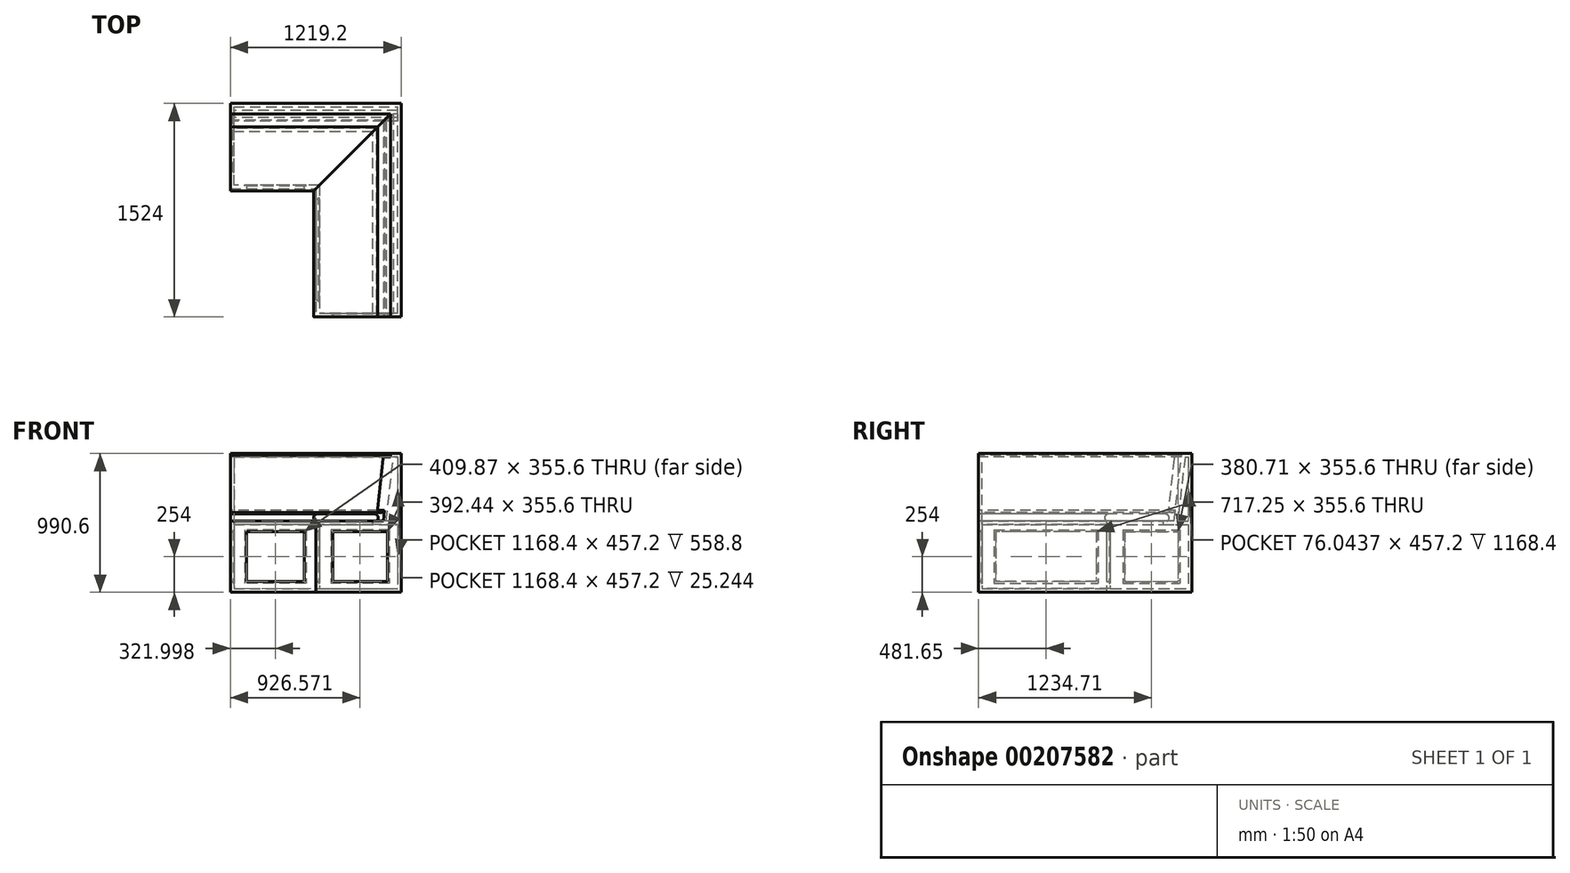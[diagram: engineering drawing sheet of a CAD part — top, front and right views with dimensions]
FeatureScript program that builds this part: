
annotation { "Feature Type Name" : "Feature", "Feature Type Description" : "" }
export const myFeature = defineFeature(function(context is Context, id is Id, definition is map)
    precondition{}
    {
        {
            var Q0;
            Q0=qCreatedBy(makeId("Top.planeOp"),FACE);
            var sketch = newSketch(context, id + "F0", { "sketchPlane" : qUnion([Q0])});
            skLineSegment(sketch, "E0", {"start": v(0, 0) * mm, "end": v(-1219.2, 0) * mm});
            skLineSegment(sketch, "E1", {"start": v(-1219.2, -609.6) * mm, "end": v(-609.6, -609.6) * mm});
            skLineSegment(sketch, "E2", {"start": v(-609.6, -609.6) * mm, "end": v(-609.6, -1524) * mm});
            skLineSegment(sketch, "E3", {"start": v(0, -1524) * mm, "end": v(0, 0) * mm});
            skLineSegment(sketch, "E4", {"start": v(-1219.2, -609.6) * mm, "end": v(-1219.2, -127) * mm});
            skLineSegment(sketch, "E5", {"start": v(-1219.2, -127) * mm, "end": v(-1219.2, 0) * mm});
            skLineSegment(sketch, "E6", {"start": v(-609.6, -1524) * mm, "end": v(-127, -1524) * mm});
            skLineSegment(sketch, "E7", {"start": v(-127, -1524) * mm, "end": v(0, -1524) * mm});
            skLineSegment(sketch, "E8", {"start": v(-1193.8, -584.2) * mm, "end": v(-584.2, -584.2) * mm});
            skLineSegment(sketch, "E9", {"start": v(-584.2, -584.2) * mm, "end": v(-584.2, -1498.6) * mm});
            skLineSegment(sketch, "E10", {"start": v(-584.2, -1498.6) * mm, "end": v(-25.4, -1498.6) * mm});
            skLineSegment(sketch, "E11", {"start": v(-25.4, -1498.6) * mm, "end": v(-25.4, -25.4) * mm});
            skLineSegment(sketch, "E12", {"start": v(-1193.8, -584.2) * mm, "end": v(-1193.8, -25.4) * mm});
            skLineSegment(sketch, "E13", {"start": v(-1193.8, -25.4) * mm, "end": v(-25.4, -25.4) * mm});
            skSolve(sketch);
        }
        {
            var Q0;
            Q0 = qSketchRegion(id + "F0", true);
            extrude(context, id + "F1", {"entities" : qUnion([Q0]), "depth" : 76.2 * mm});
        }
        {
            var Q0;
            Q0 = qSketchRegion(id + "F0", true);
            var Q1;
            Q1=makeQuery(id+"F0.imprint","IMPRINT",FACE,{"disambiguationData":[TD([[makeQuery(id+"F0.imprint","IMPRINT",EDGE,{"derivedFrom":sQuery(id+"F0.wireOp",EDGE,"E8")}),1.0]])]});
            extrude(context, id + "F2", {"entities" : qUnion([Q0, Q1]), "operationType" : NewBodyOperationType.ADD, "depth" : 25.4 * mm});
        }
        {
            var Q0;
            Q0=makeQuery(id+"F1.opExtrude","CAP_FACE",FACE,{"disambiguationData":[OSD([sQuery(id+"F0.wireOp",EDGE,"E0"),sQuery(id+"F0.wireOp",EDGE,"E1"),sQuery(id+"F0.wireOp",EDGE,"E2"),sQuery(id+"F0.wireOp",EDGE,"E3"),sQuery(id+"F0.wireOp",EDGE,"E4"),sQuery(id+"F0.wireOp",EDGE,"E5"),sQuery(id+"F0.wireOp",EDGE,"E6"),sQuery(id+"F0.wireOp",EDGE,"E7"),sQuery(id+"F0.wireOp",EDGE,"E8"),sQuery(id+"F0.wireOp",EDGE,"E9"),sQuery(id+"F0.wireOp",EDGE,"E10"),sQuery(id+"F0.wireOp",EDGE,"E11"),sQuery(id+"F0.wireOp",EDGE,"E12"),sQuery(id+"F0.wireOp",EDGE,"E13")])],"isStart":false});
            var sketch = newSketch(context, id + "F3", { "sketchPlane" : qUnion([Q0])});
            skLineSegment(sketch, "E14", {"start": v(-1219.2, -609.6) * mm, "end": v(-1219.2, -479.65) * mm});
            skLineSegment(sketch, "E15", {"start": v(-1219.2, -479.65) * mm, "end": v(-1193.8, -479.65) * mm});
            skLineSegment(sketch, "E16", {"start": v(-1193.8, -479.65) * mm, "end": v(-1193.8, -584.2) * mm});
            skLineSegment(sketch, "E17", {"start": v(-1193.8, -584.2) * mm, "end": v(-1102.14, -584.2) * mm});
            skLineSegment(sketch, "E18", {"start": v(-1102.14, -584.2) * mm, "end": v(-1102.14, -609.6) * mm});
            skLineSegment(sketch, "E19", {"start": v(-1102.14, -609.6) * mm, "end": v(-1219.2, -609.6) * mm});
            skLineSegment(sketch, "E20", {"start": v(-1219.2, 0) * mm, "end": v(-1219.2, -98.93) * mm});
            skLineSegment(sketch, "E21", {"start": v(-1219.2, -98.93) * mm, "end": v(-1193.8, -98.93) * mm});
            skLineSegment(sketch, "E22", {"start": v(-1193.8, -98.93) * mm, "end": v(-1193.8, -25.4) * mm});
            skLineSegment(sketch, "E23", {"start": v(-25.4, -25.4) * mm, "end": v(-1193.8, -25.4) * mm});
            skLineSegment(sketch, "E24", {"start": v(-609.6, -609.6) * mm, "end": v(-692.27, -609.6) * mm});
            skLineSegment(sketch, "E25", {"start": v(-692.27, -609.6) * mm, "end": v(-692.27, -584.2) * mm});
            skLineSegment(sketch, "E26", {"start": v(-692.27, -584.2) * mm, "end": v(-584.2, -584.2) * mm});
            skLineSegment(sketch, "E27", {"start": v(-584.2, -584.2) * mm, "end": v(-584.2, -683.73) * mm});
            skLineSegment(sketch, "E28", {"start": v(-584.2, -683.73) * mm, "end": v(-609.6, -683.73) * mm});
            skLineSegment(sketch, "E29", {"start": v(-609.6, -683.73) * mm, "end": v(-609.6, -609.6) * mm});
            skLineSegment(sketch, "E30", {"start": v(-609.6, -1524) * mm, "end": v(-609.6, -1400.97) * mm});
            skLineSegment(sketch, "E31", {"start": v(-609.6, -1400.97) * mm, "end": v(-584.2, -1400.97) * mm});
            skLineSegment(sketch, "E32", {"start": v(-584.2, -1400.97) * mm, "end": v(-584.2, -1498.6) * mm});
            skLineSegment(sketch, "E33", {"start": v(-584.2, -1498.6) * mm, "end": v(-488.85, -1498.6) * mm});
            skLineSegment(sketch, "E34", {"start": v(-488.85, -1498.6) * mm, "end": v(-488.85, -1524) * mm});
            skLineSegment(sketch, "E35", {"start": v(-488.85, -1524) * mm, "end": v(-609.6, -1524) * mm});
            skLineSegment(sketch, "E36", {"start": v(-25.4, -1498.6) * mm, "end": v(-96.4, -1498.6) * mm});
            skLineSegment(sketch, "E37", {"start": v(-96.4, -1498.6) * mm, "end": v(-96.4, -1524) * mm});
            skLineSegment(sketch, "E38", {"start": v(-96.4, -1524) * mm, "end": v(0, -1524) * mm});
            skLineSegment(sketch, "E39", {"start": v(-25.4, -25.4) * mm, "end": v(-25.4, -1498.6) * mm});
            skLineSegment(sketch, "E40", {"start": v(-1193.8, -25.4) * mm, "end": v(-1193.8, 0) * mm});
            skLineSegment(sketch, "E41", {"start": v(-1193.8, 0) * mm, "end": v(-1219.2, 0) * mm});
            skLineSegment(sketch, "E42", {"start": v(-25.4, -1498.6) * mm, "end": v(0, -1498.6) * mm});
            skLineSegment(sketch, "E43", {"start": v(0, -1498.6) * mm, "end": v(0, -1524) * mm});
            skLineSegment(sketch, "E44", {"start": v(0, -1498.6) * mm, "end": v(0, 0) * mm});
            skLineSegment(sketch, "E45", {"start": v(0, 0) * mm, "end": v(-25.4, 0) * mm});
            skLineSegment(sketch, "E46", {"start": v(-25.4, 0) * mm, "end": v(-25.4, -25.4) * mm});
            skLineSegment(sketch, "E47", {"start": v(-25.4, 0) * mm, "end": v(-1193.8, 0) * mm});
            skSolve(sketch);
        }
        {
            var Q0;
            Q0=makeQuery(id+"F3.imprint","IMPRINT",FACE,{"disambiguationData":[TD([[makeQuery(id+"F3.imprint","IMPRINT",EDGE,{"derivedFrom":sQuery(id+"F3.wireOp",EDGE,"E23")}),1.0]])]});
            var Q1;
            Q1=makeQuery(id+"F3.imprint","IMPRINT",FACE,{"disambiguationData":[TD([[makeQuery(id+"F3.imprint","IMPRINT",EDGE,{"derivedFrom":sQuery(id+"F3.wireOp",EDGE,"E39")}),-1.0]])]});
            extrude(context, id + "F4", {"entities" : qUnion([Q0, Q1]), "operationType" : NewBodyOperationType.ADD, "depth" : 889 * mm});
        }
        {
            var Q0;
            Q0=makeQuery(id+"F3.imprint","IMPRINT",FACE,{"disambiguationData":[TD([[makeQuery(id+"F3.imprint","IMPRINT",EDGE,{"derivedFrom":sQuery(id+"F3.wireOp",EDGE,"E14")}),-1.0]])]});
            var Q1;
            Q1=makeQuery(id+"F3.imprint","IMPRINT",FACE,{"disambiguationData":[TD([[makeQuery(id+"F3.imprint","IMPRINT",EDGE,{"derivedFrom":sQuery(id+"F3.wireOp",EDGE,"E20")}),-1.0]])]});
            var Q2;
            Q2=makeQuery(id+"F3.imprint","IMPRINT",FACE,{"disambiguationData":[TD([[makeQuery(id+"F3.imprint","IMPRINT",EDGE,{"derivedFrom":sQuery(id+"F3.wireOp",EDGE,"E24")}),1.0]])]});
            var Q3;
            Q3=makeQuery(id+"F3.imprint","IMPRINT",FACE,{"disambiguationData":[TD([[makeQuery(id+"F3.imprint","IMPRINT",EDGE,{"derivedFrom":sQuery(id+"F3.wireOp",EDGE,"E30")}),1.0]])]});
            var Q4;
            Q4=makeQuery(id+"F3.imprint","IMPRINT",FACE,{"disambiguationData":[TD([[makeQuery(id+"F3.imprint","IMPRINT",EDGE,{"derivedFrom":sQuery(id+"F3.wireOp",EDGE,"E36")}),-1.0]])]});
            extrude(context, id + "F5", {"entities" : qUnion([Q0, Q1, Q2, Q3, Q4]), "operationType" : NewBodyOperationType.ADD, "depth" : 355.6 * mm});
        }
        {
            var Q0;
            Q0=makeQuery(id+"F5.opExtrude","CAP_FACE",FACE,{"disambiguationData":[OSD([sQuery(id+"F3.wireOp",EDGE,"E24"),sQuery(id+"F3.wireOp",EDGE,"E25"),sQuery(id+"F3.wireOp",EDGE,"E26"),sQuery(id+"F3.wireOp",EDGE,"E27"),sQuery(id+"F3.wireOp",EDGE,"E28"),sQuery(id+"F3.wireOp",EDGE,"E29")])],"isStart":false});
            var sketch = newSketch(context, id + "F6", { "sketchPlane" : qUnion([Q0])});
            skLineSegment(sketch, "E48", {"start": v(-584.2, -584.2) * mm, "end": v(-1193.8, -584.2) * mm});
            skLineSegment(sketch, "E49", {"start": v(-1193.8, -584.2) * mm, "end": v(-1193.8, 0) * mm});
            skLineSegment(sketch, "E50", {"start": v(-1193.8, 0) * mm, "end": v(-1219.2, 0) * mm});
            skLineSegment(sketch, "E51", {"start": v(-1219.2, 0) * mm, "end": v(-1219.2, -609.6) * mm});
            skLineSegment(sketch, "E52", {"start": v(-1219.2, -609.6) * mm, "end": v(-609.6, -609.6) * mm});
            skLineSegment(sketch, "E53", {"start": v(-609.6, -609.6) * mm, "end": v(-609.6, -1524) * mm});
            skLineSegment(sketch, "E54", {"start": v(-609.6, -1524) * mm, "end": v(0, -1524) * mm});
            skLineSegment(sketch, "E55", {"start": v(0, -1524) * mm, "end": v(0, -1498.6) * mm});
            skLineSegment(sketch, "E56", {"start": v(0, -1498.6) * mm, "end": v(-584.2, -1498.6) * mm});
            skLineSegment(sketch, "E57", {"start": v(-584.2, -1498.6) * mm, "end": v(-584.2, -584.2) * mm});
            skSolve(sketch);
        }
        {
            var Q0;
            {var subQ1=sQuery(id+"F6.wireOp",EDGE,"E49");Q0=makeQuery(id+"F6.imprint","IMPRINT",FACE,{"disambiguationData":[TD([[makeQuery(id+"F6.imprint","IMPRINT",EDGE,{"derivedFrom":subQ1}),1.0]])]});}
            var Q1;
            {var subQ7=makeQuery(id+"F5.opExtrude","CAP_EDGE",EDGE,{"disambiguationData":[OSD([sQuery(id+"F3.wireOp",EDGE,"E25")])],"isStart":false});Q1=makeQuery(id+"F6.imprint","IMPRINT",FACE,{"disambiguationData":[TD([[makeQuery(id+"F6.imprint","IMPRINT",EDGE,{"derivedFrom":subQ7}),-1.0]])]});}
            var Q2;
            {var subQ2=sQuery(id+"F6.wireOp",EDGE,"E54");Q2=makeQuery(id+"F6.imprint","IMPRINT",FACE,{"disambiguationData":[TD([[makeQuery(id+"F6.imprint","IMPRINT",EDGE,{"derivedFrom":subQ2}),1.0]])]});}
            extrude(context, id + "F7", {"entities" : qUnion([Q0, Q1, Q2]), "operationType" : NewBodyOperationType.ADD, "depth" : 76.2 * mm});
        }
        {
            var Q0;
            Q0=makeQuery(id+"F7.boolean.opBoolean","MERGE",FACE,{"derivedFrom":[makeQuery(id+"F5.boolean.opBoolean","MERGE",FACE,{"derivedFrom":[makeQuery(id+"F1.opExtrude","SWEPT_FACE",FACE,{"disambiguationData":[OSD([sQuery(id+"F0.wireOp",EDGE,"E6"),sQuery(id+"F0.wireOp",EDGE,"E7")])]}),makeQuery(id+"F5.opExtrude","SWEPT_FACE",FACE,{"disambiguationData":[OSD([sQuery(id+"F3.wireOp",EDGE,"E35")])]}),makeQuery(id+"F5.opExtrude","SWEPT_FACE",FACE,{"disambiguationData":[OSD([sQuery(id+"F3.wireOp",EDGE,"E38")])]})]}),makeQuery(id+"F7.opExtrude","SWEPT_FACE",FACE,{"disambiguationData":[OSD([sQuery(id+"F6.wireOp",EDGE,"E54")])]})]});
            var sketch = newSketch(context, id + "F8", { "sketchPlane" : qUnion([Q0])});
            skLineSegment(sketch, "E58", {"start": v(0, 965.2) * mm, "end": v(-76.2, 965.2) * mm});
            skLineSegment(sketch, "E59", {"start": v(-76.2, 965.2) * mm, "end": v(-127, 508) * mm});
            skLineSegment(sketch, "E60", {"start": v(-127, 508) * mm, "end": v(0, 508) * mm});
            skLineSegment(sketch, "E61", {"start": v(0, 508) * mm, "end": v(0, 965.2) * mm});
            skLineSegment(sketch, "E62", {"start": v(-76.2, 965.2) * mm, "end": v(-54.4, 965.2) * mm});
            skLineSegment(sketch, "E63", {"start": v(-54.4, 965.2) * mm, "end": v(-105.2, 508) * mm});
            skLineSegment(sketch, "E64", {"start": v(-105.2, 508) * mm, "end": v(-127, 508) * mm});
            skSolve(sketch);
        }
        {
            var Q0;
            Q0 = qSketchRegion(id + "F8", true);
            extrude(context, id + "F9", {"entities" : qUnion([Q0]), "operationType" : NewBodyOperationType.ADD, "oppositeDirection" : true, "depth" : 25.4 * mm});
        }
        {
            var Q0;
            Q0=makeQuery(id+"F7.boolean.opBoolean","MERGE",FACE,{"derivedFrom":[makeQuery(id+"F5.boolean.opBoolean","MERGE",FACE,{"derivedFrom":[makeQuery(id+"F1.opExtrude","SWEPT_FACE",FACE,{"disambiguationData":[OSD([sQuery(id+"F0.wireOp",EDGE,"E4"),sQuery(id+"F0.wireOp",EDGE,"E5")])]}),makeQuery(id+"F5.opExtrude","SWEPT_FACE",FACE,{"disambiguationData":[OSD([sQuery(id+"F3.wireOp",EDGE,"E14")])]}),makeQuery(id+"F5.opExtrude","SWEPT_FACE",FACE,{"disambiguationData":[OSD([sQuery(id+"F3.wireOp",EDGE,"E20")])]})]}),makeQuery(id+"F7.opExtrude","SWEPT_FACE",FACE,{"disambiguationData":[OSD([sQuery(id+"F6.wireOp",EDGE,"E51")])]})]});
            var sketch = newSketch(context, id + "F10", { "sketchPlane" : qUnion([Q0])});
            skLineSegment(sketch, "E65", {"start": v(0, 965.2) * mm, "end": v(0, 508) * mm});
            skLineSegment(sketch, "E66", {"start": v(0, 508) * mm, "end": v(127, 508) * mm});
            skLineSegment(sketch, "E67", {"start": v(127, 508) * mm, "end": v(76.2, 965.2) * mm});
            skLineSegment(sketch, "E68", {"start": v(76.2, 965.2) * mm, "end": v(0, 965.2) * mm});
            skLineSegment(sketch, "E69", {"start": v(76.2, 965.2) * mm, "end": v(50.64, 965.2) * mm});
            skLineSegment(sketch, "E70", {"start": v(50.64, 965.2) * mm, "end": v(101.44, 508) * mm});
            skLineSegment(sketch, "E71", {"start": v(101.44, 508) * mm, "end": v(127, 508) * mm});
            skSolve(sketch);
        }
        {
            var Q0;
            Q0 = qSketchRegion(id + "F10", true);
            extrude(context, id + "F11", {"entities" : qUnion([Q0]), "operationType" : NewBodyOperationType.ADD, "oppositeDirection" : true, "depth" : 25.4 * mm});
        }
        {
            var Q0;
            Q0=makeQuery(id+"F7.opExtrude","CAP_FACE",FACE,{"disambiguationData":[OSD([sQuery(id+"F6.wireOp",EDGE,"E48"),sQuery(id+"F6.wireOp",EDGE,"E49"),sQuery(id+"F6.wireOp",EDGE,"E50"),sQuery(id+"F6.wireOp",EDGE,"E51"),sQuery(id+"F6.wireOp",EDGE,"E52"),sQuery(id+"F6.wireOp",EDGE,"E53"),sQuery(id+"F6.wireOp",EDGE,"E54"),sQuery(id+"F6.wireOp",EDGE,"E55"),sQuery(id+"F6.wireOp",EDGE,"E56"),sQuery(id+"F6.wireOp",EDGE,"E57")])],"isStart":false});
            var sketch = newSketch(context, id + "F12", { "sketchPlane" : qUnion([Q0])});
            skLineSegment(sketch, "E72", {"start": v(-1193.8, -203.2) * mm, "end": v(-1193.8, 0) * mm});
            skLineSegment(sketch, "E73", {"start": v(-1193.8, 0) * mm, "end": v(0, 0) * mm});
            skLineSegment(sketch, "E74", {"start": v(0, 0) * mm, "end": v(0, -1498.6) * mm});
            skLineSegment(sketch, "E75", {"start": v(0, -1498.6) * mm, "end": v(-203.2, -1498.6) * mm});
            skLineSegment(sketch, "E76", {"start": v(-203.2, -1498.6) * mm, "end": v(-203.2, -203.2) * mm});
            skLineSegment(sketch, "E77", {"start": v(-203.2, -203.2) * mm, "end": v(-1193.8, -203.2) * mm});
            skSolve(sketch);
        }
        {
            var Q0;
            Q0 = qSketchRegion(id + "F12", true);
            extrude(context, id + "F13", {"entities" : qUnion([Q0]), "operationType" : NewBodyOperationType.ADD, "oppositeDirection" : true, "depth" : 25.4 * mm});
        }
        {
            var Q0;
            Q0=makeQuery(id+"F10.imprint","IMPRINT",FACE,{"disambiguationData":[TD([[makeQuery(id+"F10.imprint","IMPRINT",EDGE,{"derivedFrom":sQuery(id+"F10.wireOp",EDGE,"E67")}),1.0]])]});
            var Q1;
            {var subQ0=sQuery(id+"F8.wireOp",EDGE,"E58");var subQ4=sQuery(id+"F3.wireOp",EDGE,"E39");Q1=makeQuery(id+"F13.boolean.opBoolean","SPLIT",FACE,{"disambiguationData":[TD([makeQuery(id+"F9.opExtrude","SWEPT_FACE",FACE,{"disambiguationData":[OSD([subQ0])]})])],"derivedFrom":makeQuery(id+"F4.boolean.opBoolean","MERGE",FACE,{"derivedFrom":[makeQuery(id+"F1.opExtrude","SWEPT_FACE",FACE,{"disambiguationData":[OSD([sQuery(id+"F0.wireOp",EDGE,"E11")])]}),makeQuery(id+"F4.opExtrude","SWEPT_FACE",FACE,{"disambiguationData":[OSD([subQ4])]})]})});}
            extrude(context, id + "F14", {"entities" : qUnion([Q0]), "operationType" : NewBodyOperationType.ADD, "endBound" : BoundingType.UP_TO_SURFACE, "oppositeDirection" : true, "endBoundEntityFace" : qUnion([Q1]), "depth" : 25.4 * mm});
        }
        {
            var Q0;
            Q0=makeQuery(id+"F8.imprint","IMPRINT",FACE,{"disambiguationData":[TD([[makeQuery(id+"F8.imprint","IMPRINT",EDGE,{"derivedFrom":sQuery(id+"F8.wireOp",EDGE,"E59")}),1.0]])]});
            var Q1;
            {var subQ0=sQuery(id+"F10.wireOp",EDGE,"E67");Q1=makeQuery(id+"F14.boolean.opBoolean","MERGE",FACE,{"derivedFrom":[makeQuery(id+"F11.opExtrude","SWEPT_FACE",FACE,{"disambiguationData":[OSD([subQ0])]}),makeQuery(id+"F14.opExtrude","SWEPT_FACE",FACE,{"disambiguationData":[OSD([subQ0])]})]});}
            extrude(context, id + "F15", {"entities" : qUnion([Q0]), "operationType" : NewBodyOperationType.ADD, "endBound" : BoundingType.UP_TO_SURFACE, "oppositeDirection" : true, "endBoundEntityFace" : qUnion([Q1]), "depth" : 25.4 * mm});
        }
        {
            var Q0;
            {var subQ9=sQuery(id+"F6.wireOp",EDGE,"E49");var subQ19=sQuery(id+"F0.wireOp",EDGE,"E8");var subQ21=sQuery(id+"F0.wireOp",EDGE,"E12");var subQ27=sQuery(id+"F10.wireOp",EDGE,"E65");Q0=makeQuery(id+"F13.boolean.opBoolean","SPLIT",FACE,{"disambiguationData":[TD([makeQuery(id+"F1.opExtrude","SWEPT_FACE",FACE,{"disambiguationData":[OSD([subQ19])]})])],"derivedFrom":makeQuery(id+"F11.boolean.opBoolean","MERGE",FACE,{"derivedFrom":[makeQuery(id+"F7.boolean.opBoolean","MERGE",FACE,{"derivedFrom":[makeQuery(id+"F5.boolean.opBoolean","MERGE",FACE,{"derivedFrom":[makeQuery(id+"F1.opExtrude","SWEPT_FACE",FACE,{"disambiguationData":[OSD([subQ21])]}),makeQuery(id+"F5.opExtrude","SWEPT_FACE",FACE,{"disambiguationData":[OSD([sQuery(id+"F3.wireOp",EDGE,"E16")])]}),makeQuery(id+"F5.opExtrude","SWEPT_FACE",FACE,{"disambiguationData":[OSD([sQuery(id+"F3.wireOp",EDGE,"E22"),sQuery(id+"F3.wireOp",EDGE,"E40")])]})]}),makeQuery(id+"F7.opExtrude","SWEPT_FACE",FACE,{"disambiguationData":[OSD([subQ9])]})]}),makeQuery(id+"F11.opExtrude","CAP_FACE",FACE,{"disambiguationData":[OSD([subQ27,sQuery(id+"F10.wireOp",EDGE,"E66"),sQuery(id+"F10.wireOp",EDGE,"E67"),sQuery(id+"F10.wireOp",EDGE,"E68"),sQuery(id+"F10.wireOp",EDGE,"E69"),sQuery(id+"F10.wireOp",EDGE,"E71")])],"isStart":false})]})});}
            var sketch = newSketch(context, id + "F16", { "sketchPlane" : qUnion([Q0])});
            skLineSegment(sketch, "E78.bottom", {"start": v(-492.35, 444.5) * mm, "end": v(-86.23, 444.5) * mm});
            skLineSegment(sketch, "E78.top", {"start": v(-492.35, 63.5) * mm, "end": v(-86.23, 63.5) * mm});
            skLineSegment(sketch, "E78.left", {"start": v(-492.35, 444.5) * mm, "end": v(-492.35, 63.5) * mm});
            skLineSegment(sketch, "E78.right", {"start": v(-86.23, 444.5) * mm, "end": v(-86.23, 63.5) * mm});
            skSolve(sketch);
        }
        {
            var Q0;
            {var subQ0=sQuery(id+"F0.wireOp",EDGE,"E12");Q0=makeQuery(id+"F16.imprint","IMPRINT",FACE,{"disambiguationData":[TD([[makeQuery(id+"F16.imprint","IMPRINT",EDGE,{"derivedFrom":makeQuery(id+"F1.opExtrude","CAP_EDGE",EDGE,{"disambiguationData":[OSD([subQ0])],"isStart":false})}),1.0]])]});}
            var Q1;
            Q1=makeQuery(id+"F16.imprint","IMPRINT",FACE,{"disambiguationData":[TD([[makeQuery(id+"F16.imprint","IMPRINT",EDGE,{"derivedFrom":sQuery(id+"F16.wireOp",EDGE,"E78.bottom")}),-1.0]])]});
            extrude(context, id + "F17", {"entities" : qUnion([Q0, Q1]), "oppositeDirection" : true, "depth" : 6.35 * mm});
        }
        {
            var Q0;
            Q0=makeQuery(id+"F7.boolean.opBoolean","MERGE",FACE,{"derivedFrom":[makeQuery(id+"F5.boolean.opBoolean","MERGE",FACE,{"derivedFrom":[makeQuery(id+"F1.opExtrude","SWEPT_FACE",FACE,{"disambiguationData":[OSD([sQuery(id+"F0.wireOp",EDGE,"E8")])]}),makeQuery(id+"F5.opExtrude","SWEPT_FACE",FACE,{"disambiguationData":[OSD([sQuery(id+"F3.wireOp",EDGE,"E17")])]}),makeQuery(id+"F5.opExtrude","SWEPT_FACE",FACE,{"disambiguationData":[OSD([sQuery(id+"F3.wireOp",EDGE,"E26")])]})]}),makeQuery(id+"F7.opExtrude","SWEPT_FACE",FACE,{"disambiguationData":[OSD([sQuery(id+"F6.wireOp",EDGE,"E48")])]})]});
            var sketch = newSketch(context, id + "F18", { "sketchPlane" : qUnion([Q0])});
            skLineSegment(sketch, "E79.bottom", {"start": v(679.57, 444.5) * mm, "end": v(1114.84, 444.5) * mm});
            skLineSegment(sketch, "E79.top", {"start": v(679.57, 63.5) * mm, "end": v(1114.84, 63.5) * mm});
            skLineSegment(sketch, "E79.left", {"start": v(679.57, 444.5) * mm, "end": v(679.57, 63.5) * mm});
            skLineSegment(sketch, "E79.right", {"start": v(1114.84, 444.5) * mm, "end": v(1114.84, 63.5) * mm});
            skSolve(sketch);
        }
        {
            var Q0;
            {var subQ0=sQuery(id+"F0.wireOp",EDGE,"E8");Q0=makeQuery(id+"F18.imprint","IMPRINT",FACE,{"disambiguationData":[TD([[makeQuery(id+"F18.imprint","IMPRINT",EDGE,{"derivedFrom":makeQuery(id+"F1.opExtrude","CAP_EDGE",EDGE,{"disambiguationData":[OSD([subQ0])],"isStart":false})}),-1.0]])]});}
            var Q1;
            Q1=makeQuery(id+"F18.imprint","IMPRINT",FACE,{"disambiguationData":[TD([[makeQuery(id+"F18.imprint","IMPRINT",EDGE,{"derivedFrom":sQuery(id+"F18.wireOp",EDGE,"E79.bottom")}),-1.0]])]});
            extrude(context, id + "F19", {"entities" : qUnion([Q0, Q1]), "oppositeDirection" : true, "depth" : 6.35 * mm});
        }
        {
            var Q0;
            Q0=makeQuery(id+"F7.boolean.opBoolean","MERGE",FACE,{"derivedFrom":[makeQuery(id+"F5.boolean.opBoolean","MERGE",FACE,{"derivedFrom":[makeQuery(id+"F1.opExtrude","SWEPT_FACE",FACE,{"disambiguationData":[OSD([sQuery(id+"F0.wireOp",EDGE,"E9")])]}),makeQuery(id+"F5.opExtrude","SWEPT_FACE",FACE,{"disambiguationData":[OSD([sQuery(id+"F3.wireOp",EDGE,"E27")])]}),makeQuery(id+"F5.opExtrude","SWEPT_FACE",FACE,{"disambiguationData":[OSD([sQuery(id+"F3.wireOp",EDGE,"E32")])]})]}),makeQuery(id+"F7.opExtrude","SWEPT_FACE",FACE,{"disambiguationData":[OSD([sQuery(id+"F6.wireOp",EDGE,"E57")])]})]});
            var sketch = newSketch(context, id + "F20", { "sketchPlane" : qUnion([Q0])});
            skLineSegment(sketch, "E80.bottom", {"start": v(-1413.67, 444.5) * mm, "end": v(-671.03, 444.5) * mm});
            skLineSegment(sketch, "E80.top", {"start": v(-1413.67, 63.5) * mm, "end": v(-671.03, 63.5) * mm});
            skLineSegment(sketch, "E80.left", {"start": v(-1413.67, 444.5) * mm, "end": v(-1413.67, 63.5) * mm});
            skLineSegment(sketch, "E80.right", {"start": v(-671.03, 444.5) * mm, "end": v(-671.03, 63.5) * mm});
            skSolve(sketch);
        }
        {
            var Q0;
            {var subQ0=sQuery(id+"F0.wireOp",EDGE,"E9");Q0=makeQuery(id+"F20.imprint","IMPRINT",FACE,{"disambiguationData":[TD([[makeQuery(id+"F20.imprint","IMPRINT",EDGE,{"derivedFrom":makeQuery(id+"F1.opExtrude","CAP_EDGE",EDGE,{"disambiguationData":[OSD([subQ0])],"isStart":false})}),-1.0]])]});}
            var Q1;
            Q1=makeQuery(id+"F20.imprint","IMPRINT",FACE,{"disambiguationData":[TD([[makeQuery(id+"F20.imprint","IMPRINT",EDGE,{"derivedFrom":sQuery(id+"F20.wireOp",EDGE,"E80.bottom")}),-1.0]])]});
            extrude(context, id + "F21", {"entities" : qUnion([Q0, Q1]), "oppositeDirection" : true, "depth" : 6.35 * mm});
        }
        {
            var Q0;
            {var subQ0=sQuery(id+"F0.wireOp",EDGE,"E9");var subQ8=sQuery(id+"F0.wireOp",EDGE,"E10");var subQ18=sQuery(id+"F6.wireOp",EDGE,"E56");var subQ27=sQuery(id+"F8.wireOp",EDGE,"E61");Q0=makeQuery(id+"F13.boolean.opBoolean","SPLIT",FACE,{"disambiguationData":[TD([makeQuery(id+"F1.opExtrude","SWEPT_FACE",FACE,{"disambiguationData":[OSD([subQ0])]})])],"derivedFrom":makeQuery(id+"F9.boolean.opBoolean","MERGE",FACE,{"derivedFrom":[makeQuery(id+"F7.boolean.opBoolean","MERGE",FACE,{"derivedFrom":[makeQuery(id+"F5.boolean.opBoolean","MERGE",FACE,{"derivedFrom":[makeQuery(id+"F1.opExtrude","SWEPT_FACE",FACE,{"disambiguationData":[OSD([subQ8])]}),makeQuery(id+"F5.opExtrude","SWEPT_FACE",FACE,{"disambiguationData":[OSD([sQuery(id+"F3.wireOp",EDGE,"E33")])]}),makeQuery(id+"F5.opExtrude","SWEPT_FACE",FACE,{"disambiguationData":[OSD([sQuery(id+"F3.wireOp",EDGE,"E36"),sQuery(id+"F3.wireOp",EDGE,"E42")])]})]}),makeQuery(id+"F7.opExtrude","SWEPT_FACE",FACE,{"disambiguationData":[OSD([subQ18])]})]}),makeQuery(id+"F9.opExtrude","CAP_FACE",FACE,{"disambiguationData":[OSD([sQuery(id+"F8.wireOp",EDGE,"E58"),sQuery(id+"F8.wireOp",EDGE,"E59"),sQuery(id+"F8.wireOp",EDGE,"E60"),subQ27,sQuery(id+"F8.wireOp",EDGE,"E62"),sQuery(id+"F8.wireOp",EDGE,"E64")])],"isStart":false})]})});}
            var sketch = newSketch(context, id + "F22", { "sketchPlane" : qUnion([Q0])});
            skLineSegment(sketch, "E81.bottom", {"start": v(83.7, 444.5) * mm, "end": v(501.55, 444.5) * mm});
            skLineSegment(sketch, "E81.top", {"start": v(83.7, 63.5) * mm, "end": v(501.55, 63.5) * mm});
            skLineSegment(sketch, "E81.left", {"start": v(83.7, 444.5) * mm, "end": v(83.7, 63.5) * mm});
            skLineSegment(sketch, "E81.right", {"start": v(501.55, 444.5) * mm, "end": v(501.55, 63.5) * mm});
            skSolve(sketch);
        }
        {
            var Q0;
            {var subQ0=sQuery(id+"F0.wireOp",EDGE,"E10");Q0=makeQuery(id+"F22.imprint","IMPRINT",FACE,{"disambiguationData":[TD([[makeQuery(id+"F22.imprint","IMPRINT",EDGE,{"derivedFrom":makeQuery(id+"F1.opExtrude","CAP_EDGE",EDGE,{"disambiguationData":[OSD([subQ0])],"isStart":false})}),-1.0]])]});}
            var Q1;
            Q1=makeQuery(id+"F22.imprint","IMPRINT",FACE,{"disambiguationData":[TD([[makeQuery(id+"F22.imprint","IMPRINT",EDGE,{"derivedFrom":sQuery(id+"F22.wireOp",EDGE,"E81.bottom")}),-1.0]])]});
            extrude(context, id + "F23", {"entities" : qUnion([Q0, Q1]), "oppositeDirection" : true, "depth" : 6.35 * mm});
        }
        {
            var Q0;
            {var subQ6=sQuery(id+"F6.wireOp",EDGE,"E57");var subQ8=sQuery(id+"F6.wireOp",EDGE,"E51");var subQ9=sQuery(id+"F12.wireOp",EDGE,"E77");var subQ15=sQuery(id+"F6.wireOp",EDGE,"E53");var subQ16=sQuery(id+"F6.wireOp",EDGE,"E48");var subQ17=sQuery(id+"F6.wireOp",EDGE,"E49");var subQ18=sQuery(id+"F6.wireOp",EDGE,"E52");var subQ19=sQuery(id+"F6.wireOp",EDGE,"E54");var subQ20=sQuery(id+"F6.wireOp",EDGE,"E56");var subQ21=sQuery(id+"F12.wireOp",EDGE,"E76");Q0=makeQuery(id+"F15.boolean.opBoolean","SPLIT",FACE,{"disambiguationData":[TD([makeQuery(id+"F1.opExtrude","SWEPT_FACE",FACE,{"disambiguationData":[OSD([sQuery(id+"F0.wireOp",EDGE,"E1")])]})])],"derivedFrom":makeQuery(id+"F13.boolean.opBoolean","MERGE",FACE,{"derivedFrom":[makeQuery(id+"F7.opExtrude","CAP_FACE",FACE,{"disambiguationData":[OSD([subQ16,subQ17,sQuery(id+"F6.wireOp",EDGE,"E50"),subQ8,subQ18,subQ15,subQ19,sQuery(id+"F6.wireOp",EDGE,"E55"),subQ20,subQ6])],"isStart":false}),makeQuery(id+"F13.opExtrude","CAP_FACE",FACE,{"disambiguationData":[OSD([sQuery(id+"F12.wireOp",EDGE,"E72"),sQuery(id+"F12.wireOp",EDGE,"E73"),sQuery(id+"F12.wireOp",EDGE,"E74"),sQuery(id+"F12.wireOp",EDGE,"E75"),subQ21,subQ9])],"isStart":true})]})});}
            var sketch = newSketch(context, id + "F24", { "sketchPlane" : qUnion([Q0])});
            skLineSegment(sketch, "E82", {"start": v(-1193.8, -203.2) * mm, "end": v(-1193.8, -584.2) * mm});
            skLineSegment(sketch, "E83", {"start": v(-1193.8, -584.2) * mm, "end": v(-584.2, -584.2) * mm});
            skLineSegment(sketch, "E84", {"start": v(-584.2, -584.2) * mm, "end": v(-203.2, -203.2) * mm});
            skLineSegment(sketch, "E85", {"start": v(-203.2, -203.2) * mm, "end": v(-1193.8, -203.2) * mm});
            skLineSegment(sketch, "E86", {"start": v(-584.2, -584.2) * mm, "end": v(-584.2, -1498.6) * mm});
            skLineSegment(sketch, "E87", {"start": v(-584.2, -1498.6) * mm, "end": v(-203.2, -1498.6) * mm});
            skLineSegment(sketch, "E88", {"start": v(-203.2, -1498.6) * mm, "end": v(-203.2, -203.2) * mm});
            skSolve(sketch);
        }
        {
            var Q0;
            Q0=makeQuery(id+"F24.imprint","IMPRINT",FACE,{"disambiguationData":[TD([[makeQuery(id+"F24.imprint","IMPRINT",EDGE,{"derivedFrom":sQuery(id+"F24.wireOp",EDGE,"E82")}),-1.0]])]});
            extrude(context, id + "F25", {"entities" : qUnion([Q0]), "oppositeDirection" : true, "depth" : 25.4 * mm});
        }
        {
            var Q0;
            Q0=makeQuery(id+"F24.imprint","IMPRINT",FACE,{"disambiguationData":[TD([[makeQuery(id+"F24.imprint","IMPRINT",EDGE,{"derivedFrom":sQuery(id+"F24.wireOp",EDGE,"E84")}),-1.0]])]});
            extrude(context, id + "F26", {"entities" : qUnion([Q0]), "oppositeDirection" : true, "depth" : 25.4 * mm});
        }
        {
            var Q0;
            Q0=makeQuery(id+"F9.boolean.opBoolean","MERGE",FACE,{"derivedFrom":[makeQuery(id+"F7.boolean.opBoolean","MERGE",FACE,{"derivedFrom":[makeQuery(id+"F5.boolean.opBoolean","MERGE",FACE,{"derivedFrom":[makeQuery(id+"F1.opExtrude","SWEPT_FACE",FACE,{"disambiguationData":[OSD([sQuery(id+"F0.wireOp",EDGE,"E6"),sQuery(id+"F0.wireOp",EDGE,"E7")])]}),makeQuery(id+"F5.opExtrude","SWEPT_FACE",FACE,{"disambiguationData":[OSD([sQuery(id+"F3.wireOp",EDGE,"E35")])]}),makeQuery(id+"F5.opExtrude","SWEPT_FACE",FACE,{"disambiguationData":[OSD([sQuery(id+"F3.wireOp",EDGE,"E38")])]})]}),makeQuery(id+"F7.opExtrude","SWEPT_FACE",FACE,{"disambiguationData":[OSD([sQuery(id+"F6.wireOp",EDGE,"E54")])]})]}),makeQuery(id+"F9.opExtrude","CAP_FACE",FACE,{"disambiguationData":[OSD([sQuery(id+"F8.wireOp",EDGE,"E58"),sQuery(id+"F8.wireOp",EDGE,"E59"),sQuery(id+"F8.wireOp",EDGE,"E60"),sQuery(id+"F8.wireOp",EDGE,"E61"),sQuery(id+"F8.wireOp",EDGE,"E62"),sQuery(id+"F8.wireOp",EDGE,"E64")])],"isStart":true})]});
            var sketch = newSketch(context, id + "F27", { "sketchPlane" : qUnion([Q0])});
            skLineSegment(sketch, "E89", {"start": v(-609.6, 508) * mm, "end": v(-177.8, 508) * mm});
            skLineSegment(sketch, "E90", {"start": v(-596.9, 558.8) * mm, "end": v(-190.5, 558.8) * mm});
            skArc(sketch, "E91", {"start": v(-596.9, 558.8) * mm, "mid": v(-623.08, 538.36) * mm, "end": v(-609.6, 508) * mm});
            skArc(sketch, "E92", {"start": v(-177.8, 508) * mm, "mid": v(-164.32, 538.36) * mm, "end": v(-190.5, 558.8) * mm});
            skLineSegment(sketch, "E93", {"start": v(-76.2, 965.2) * mm, "end": v(-118.27, 586.53) * mm});
            skLineSegment(sketch, "E94", {"start": v(-128.72, 952.5) * mm, "end": v(-168, 599.07) * mm});
            skArc(sketch, "E95", {"start": v(-76.2, 965.2) * mm, "mid": v(-106.91, 977.26) * mm, "end": v(-128.72, 952.5) * mm});
            skArc(sketch, "E96", {"start": v(-168, 599.07) * mm, "mid": v(-148.6, 571.12) * mm, "end": v(-118.27, 586.53) * mm});
            skSolve(sketch);
        }
        {
            var Q0;
            Q0=makeQuery(id+"F27.imprint","IMPRINT",FACE,{"disambiguationData":[TD([[makeQuery(id+"F27.imprint","IMPRINT",EDGE,{"derivedFrom":sQuery(id+"F27.wireOp",EDGE,"E89")}),1.0]])]});
            var Q1;
            Q1=makeQuery(id+"F27.imprint","IMPRINT",FACE,{"disambiguationData":[TD([[makeQuery(id+"F27.imprint","IMPRINT",EDGE,{"derivedFrom":sQuery(id+"F27.wireOp",EDGE,"E93")}),-1.0]])]});
            var Q2;
            Q2=makeQuery(id+"F25.opExtrude","SWEPT_FACE",FACE,{"disambiguationData":[OSD([sQuery(id+"F24.wireOp",EDGE,"E84")])]});
            extrude(context, id + "F28", {"entities" : qUnion([Q0, Q1]), "endBound" : BoundingType.UP_TO_SURFACE, "oppositeDirection" : true, "endBoundEntityFace" : qUnion([Q2]), "depth" : 25.4 * mm});
        }
        {
            var Q0;
            Q0=makeQuery(id+"F11.boolean.opBoolean","MERGE",FACE,{"derivedFrom":[makeQuery(id+"F7.boolean.opBoolean","MERGE",FACE,{"derivedFrom":[makeQuery(id+"F5.boolean.opBoolean","MERGE",FACE,{"derivedFrom":[makeQuery(id+"F1.opExtrude","SWEPT_FACE",FACE,{"disambiguationData":[OSD([sQuery(id+"F0.wireOp",EDGE,"E4"),sQuery(id+"F0.wireOp",EDGE,"E5")])]}),makeQuery(id+"F5.opExtrude","SWEPT_FACE",FACE,{"disambiguationData":[OSD([sQuery(id+"F3.wireOp",EDGE,"E14")])]}),makeQuery(id+"F5.opExtrude","SWEPT_FACE",FACE,{"disambiguationData":[OSD([sQuery(id+"F3.wireOp",EDGE,"E20")])]})]}),makeQuery(id+"F7.opExtrude","SWEPT_FACE",FACE,{"disambiguationData":[OSD([sQuery(id+"F6.wireOp",EDGE,"E51")])]})]}),makeQuery(id+"F11.opExtrude","CAP_FACE",FACE,{"disambiguationData":[OSD([sQuery(id+"F10.wireOp",EDGE,"E65"),sQuery(id+"F10.wireOp",EDGE,"E66"),sQuery(id+"F10.wireOp",EDGE,"E67"),sQuery(id+"F10.wireOp",EDGE,"E68"),sQuery(id+"F10.wireOp",EDGE,"E69"),sQuery(id+"F10.wireOp",EDGE,"E71")])],"isStart":true})]});
            var sketch = newSketch(context, id + "F29", { "sketchPlane" : qUnion([Q0])});
            skLineSegment(sketch, "E97", {"start": v(609.6, 508) * mm, "end": v(177.8, 508) * mm});
            skLineSegment(sketch, "E98", {"start": v(190.5, 558.8) * mm, "end": v(596.9, 558.8) * mm});
            skArc(sketch, "E99", {"start": v(190.5, 558.8) * mm, "mid": v(164.32, 538.36) * mm, "end": v(177.8, 508) * mm});
            skArc(sketch, "E100", {"start": v(609.6, 508) * mm, "mid": v(623.08, 538.36) * mm, "end": v(596.9, 558.8) * mm});
            skLineSegment(sketch, "E101", {"start": v(76.2, 965.2) * mm, "end": v(118.27, 586.53) * mm});
            skLineSegment(sketch, "E102", {"start": v(128.72, 952.5) * mm, "end": v(168, 599.07) * mm});
            skArc(sketch, "E103", {"start": v(128.72, 952.5) * mm, "mid": v(106.91, 977.26) * mm, "end": v(76.2, 965.2) * mm});
            skArc(sketch, "E104", {"start": v(118.27, 586.53) * mm, "mid": v(148.6, 571.12) * mm, "end": v(168, 599.07) * mm});
            skSolve(sketch);
        }
        {
            var Q0;
            Q0=makeQuery(id+"F29.imprint","IMPRINT",FACE,{"disambiguationData":[TD([[makeQuery(id+"F29.imprint","IMPRINT",EDGE,{"derivedFrom":sQuery(id+"F29.wireOp",EDGE,"E97")}),1.0]])]});
            var Q1;
            Q1=makeQuery(id+"F29.imprint","IMPRINT",FACE,{"disambiguationData":[TD([[makeQuery(id+"F29.imprint","IMPRINT",EDGE,{"derivedFrom":sQuery(id+"F29.wireOp",EDGE,"E101")}),-1.0]])]});
            var Q2;
            Q2=makeQuery(id+"F26.opExtrude","SWEPT_FACE",FACE,{"disambiguationData":[OSD([sQuery(id+"F24.wireOp",EDGE,"E84")])]});
            extrude(context, id + "F30", {"entities" : qUnion([Q0, Q1]), "endBound" : BoundingType.UP_TO_SURFACE, "oppositeDirection" : true, "endBoundEntityFace" : qUnion([Q2]), "depth" : 25.4 * mm});
        }
        {
            var Q0;
            {var subQ0=sQuery(id+"F8.wireOp",EDGE,"E62");var subQ1=sQuery(id+"F10.wireOp",EDGE,"E69");Q0=makeQuery(id+"F15.boolean.opBoolean","MERGE",FACE,{"derivedFrom":[makeQuery(id+"F14.boolean.opBoolean","MERGE",FACE,{"derivedFrom":[makeQuery(id+"F11.boolean.opBoolean","MERGE",FACE,{"derivedFrom":[makeQuery(id+"F9.boolean.opBoolean","MERGE",FACE,{"derivedFrom":[makeQuery(id+"F4.opExtrude","CAP_FACE",FACE,{"disambiguationData":[OSD([sQuery(id+"F3.wireOp",EDGE,"E23"),sQuery(id+"F3.wireOp",EDGE,"E39"),sQuery(id+"F3.wireOp",EDGE,"E40"),sQuery(id+"F3.wireOp",EDGE,"E42"),sQuery(id+"F3.wireOp",EDGE,"E44"),sQuery(id+"F3.wireOp",EDGE,"E45"),sQuery(id+"F3.wireOp",EDGE,"E47")])],"isStart":false}),makeQuery(id+"F9.opExtrude","SWEPT_FACE",FACE,{"disambiguationData":[OSD([sQuery(id+"F8.wireOp",EDGE,"E58"),subQ0])]})]}),makeQuery(id+"F11.opExtrude","SWEPT_FACE",FACE,{"disambiguationData":[OSD([sQuery(id+"F10.wireOp",EDGE,"E68"),subQ1])]})]}),makeQuery(id+"F14.opExtrude","SWEPT_FACE",FACE,{"disambiguationData":[OSD([subQ1])]})]}),makeQuery(id+"F15.opExtrude","SWEPT_FACE",FACE,{"disambiguationData":[OSD([subQ0])]})]});}
            var sketch = newSketch(context, id + "F31", { "sketchPlane" : qUnion([Q0])});
            skLineSegment(sketch, "E105", {"start": v(-1219.2, 0) * mm, "end": v(-1219.2, -76.2) * mm});
            skLineSegment(sketch, "E106", {"start": v(-1219.2, -76.2) * mm, "end": v(-76.2, -76.2) * mm});
            skLineSegment(sketch, "E107", {"start": v(-76.2, -76.2) * mm, "end": v(-76.2, -1524) * mm});
            skLineSegment(sketch, "E108", {"start": v(-76.2, -1524) * mm, "end": v(0, -1524) * mm});
            skLineSegment(sketch, "E109", {"start": v(0, -1524) * mm, "end": v(0, 0) * mm});
            skLineSegment(sketch, "E110", {"start": v(0, 0) * mm, "end": v(-1219.2, 0) * mm});
            skSolve(sketch);
        }
        {
            var Q0;
            Q0 = qSketchRegion(id + "F31", true);
            extrude(context, id + "F32", {"entities" : qUnion([Q0]), "operationType" : NewBodyOperationType.ADD, "depth" : 25.4 * mm});
        }
    });
